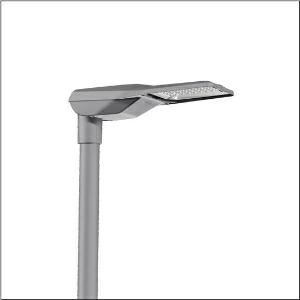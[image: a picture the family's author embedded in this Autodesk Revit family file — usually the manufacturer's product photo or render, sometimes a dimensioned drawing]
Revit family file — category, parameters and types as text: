
# Revit family: streetlight_sl_21_iq_mini___pl52_5xe2h31d08hb_f62b
name_source: partatom
category: Lighting Fixtures
units: mm (PartAtom-declared; Revit-internal decimal feet)

## family parameters
Cut with Voids When Loaded = No
Host = Face
Light Source = No
Part Type = Normal
Room Calculation Point = No
Round Connector Dimension = Use Diameter
Shared = No

## types (1)
- --- (1 x LED, 9290 lm, 70.9 W, 3000K)
    Apparent Load = 71 VA
    CIE Flux Codes = 27 59 98 100 100
    Color Rendering = 70
    Color Temperature = 3000K
    Default Elevation = 1800 mm
    Description = Streetlight SL 21 iQ mini, mast luminaire, primary light control with lens, of PMMA, primary optical cover: cover, of toughened safety glass, transparent, light distribution: PL52, light emission: direct distribution, primary light characteristic: asymmetric, installation type: post-top, side-entry, LED, High Power LED, rated luminous flux: 9.290lm, luminous efficacy: 131lm/W, light colour: 730, colour temperature: 3000K, control gear: iQ-Comfort, control: Auto-Match, Temp-Guard, Lumen-Switch, Night-Set, Smart-Wire, Light-Fading, Desk-Remote (wireless, voltage-free reading and setting of iQ features in the workshop via application-optimized NFC function/RFID function), optimised constant luminous flux control (CLO 2.0), pre-setting: linear dimming characteristic, mains connection: 220..240V, AC, 50/60Hz, start of lifetime: 71W, end of service life: 75W, reduction: 31W, luminaire housing, of diecast aluminium, powder-coated, SITECO metallic grey (DB 702S), corrosivity category C5 high according to DIN EN ISO 12944, please order mast flange separately, inclination adjustable: 0°, 5°, 10°, 15°, sealing non-destructively replaceable, multi-level sealing system, length: 628mm, width: 235mm, height: 110mm, mast flange for spigot size: 42mm (side-entry): 5XC10008XM4, 60/48mm (side-entry/post-top): 5XC10108XM2, 76/60mm (side-entry/post-top): 5XC10108XM1, mounting height: 4..8m, protection rating (complete): IP66, insulation class (complete): insulation class II (safety insulation), certification: CE, ENEC, ENEC+, VDE, impact resistance: IK10, permissible operating ambient temperature for outdoor applications: -40..+50°C, standard-compliant lighting for roads and squares, packaging unit: 1 piece

Light Distribution: PL52
    Height = 110 mm
    Lamp = 1 x LED
    Lamp Light Flux = 9290 lm
    Lamp Power = 70.9 W
    Lamp count = 1
    Length = 625 mm
    Luminous efficacy = 131 lm/W
    Manufacturer = Siteco
    ModVariant = No
    Model = 5XE2H31D08HB
    Mounting Place = Pole
    Mounting Type = Pole top
    Number of Poles = 1
    OnlyDefault = Yes
    Power Factor = 1
    Product Name = Streetlight SL 21 iQ mini | PL52
    Product group = mast luminaire | pylon top
    ProductGroupID = 6100
    Protection Class = Protection class II
    Protection Degree = IP 66
    RLX_Detail_Level = 1
    RLX_Emergency_Light_Flux = 0 lm
    RLX_Emergency_Type = 0
    RLX_Emergency_Type_DB = No
    RlxData = <blob elided: 35969 chars, md5=26aff759>
    Socket = socket
    Standby Power = 0 W
    System Light Flux = 9290 lm
    System Power = 71 W
    Type Comments = factory setting: luminous flux: 100 % | dim-lin: 254 | 711 mA
    Type Image = l_1003519.jpg
    URL = http://relux.com
    VarID = @adj_159501
    Voltage = 0 V
    Weight = 0.00 kg
    Width = 234 mm

## geometry (parser evidence)
native form markers: Blend x4, Sweep x10
no freeform markers — native parametric forms only
